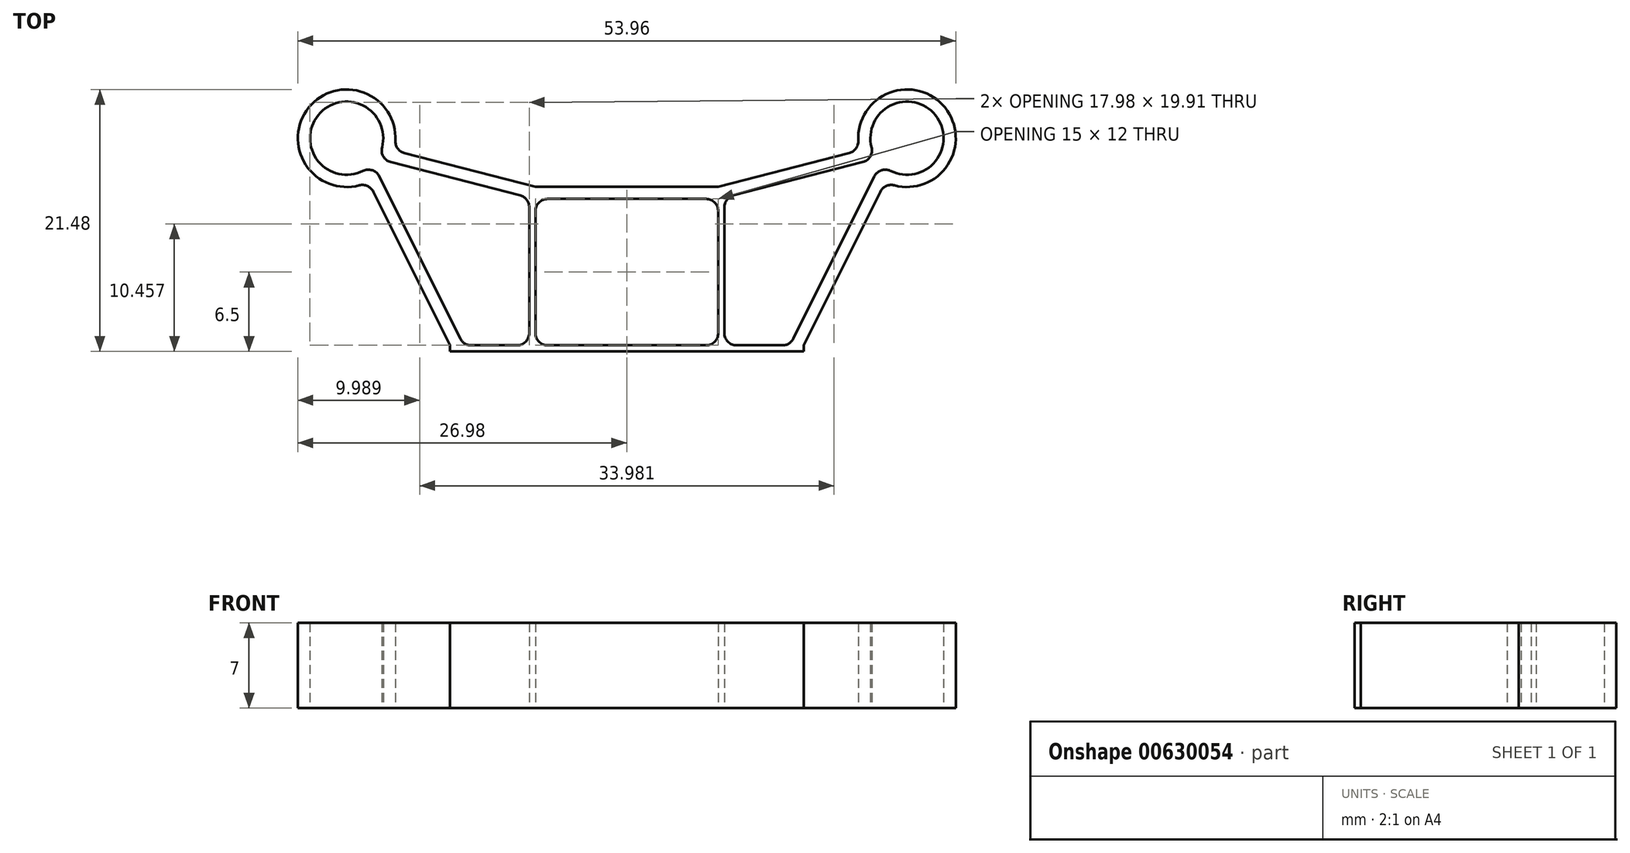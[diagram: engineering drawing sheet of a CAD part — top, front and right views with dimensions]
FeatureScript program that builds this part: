
annotation { "Feature Type Name" : "Feature", "Feature Type Description" : "" }
export const myFeature = defineFeature(function(context is Context, id is Id, definition is map)
    precondition{}
    {
        {
            var Q0;
            Q0=qCreatedBy(makeId("Top.planeOp"),FACE);
            var sketch = newSketch(context, id + "F0", { "sketchPlane" : qUnion([Q0])});
            skCircle(sketch, "E0", {"center": v(0, 0) * mm, "radius": 32.5 * mm, "construction": true});
            skLineSegment(sketch, "E1", {"start": v(0, 0) * mm, "end": v(35.36, 35.36) * mm, "construction": true});
            skArc(sketch, "E2", {"start": v(20.82, 20.9) * mm, "mid": v(25.31, 24.87) * mm, "end": v(20.5, 21.3) * mm});
            skArc(sketch, "E3.0", {"start": v(21.2, 19.4) * mm, "mid": v(26.1, 25.5) * mm, "end": v(19.1, 21.98) * mm});
            skLineSegment(sketch, "E4.bottom", {"start": v(22.5, -5.5) * mm, "end": v(-22.5, -5.5) * mm, "construction": true});
            skLineSegment(sketch, "E4.top", {"start": v(14.5, 5.5) * mm, "end": v(0, 5.5) * mm});
            skLineSegment(sketch, "E4.left", {"start": v(22.5, -5.5) * mm, "end": v(22.5, 6) * mm, "construction": true});
            skLineSegment(sketch, "E4.right", {"start": v(-22.5, -5.5) * mm, "end": v(-22.5, 5.5) * mm, "construction": true});
            skLineSegment(sketch, "E5.0", {"start": v(14.5, -5.5) * mm, "end": v(14.5, 6) * mm, "construction": true});
            skLineSegment(sketch, "E6.0", {"start": v(14.5, 6) * mm, "end": v(0, 6) * mm});
            skLineSegment(sketch, "E7", {"start": v(0, 0) * mm, "end": v(0, 47.28) * mm, "construction": true});
            skPoint(sketch, "E7.endSnap0", {"position": v(0, 18) * mm});
            skLineSegment(sketch, "E8.0", {"start": v(7.5, 0) * mm, "end": v(7.5, 5.5) * mm, "construction": true});
            skLineSegment(sketch, "E9", {"start": v(14.5, 6) * mm, "end": v(21.2, 19.4) * mm});
            skLineSegment(sketch, "E10", {"start": v(7.5, 19) * mm, "end": v(19.1, 21.98) * mm});
            skLineSegment(sketch, "E11.0", {"start": v(13.38, 6) * mm, "end": v(20.82, 20.9) * mm});
            skLineSegment(sketch, "E12.trimOffspring", {"start": v(7.5, 19) * mm, "end": v(0, 19) * mm});
            skLineSegment(sketch, "E13.trimOffspring", {"start": v(7.63, 18) * mm, "end": v(0, 18) * mm});
            skPoint(sketch, "E14.0.start.orphan", {"position": v(22.5, 18) * mm});
            skPoint(sketch, "E15.orphan", {"position": v(-22.5, 18) * mm});
            skLineSegment(sketch, "E16", {"start": v(0, 18) * mm, "end": v(0, 19) * mm});
            skPoint(sketch, "E17.orphan", {"position": v(22.5, 5.5) * mm});
            skLineSegment(sketch, "E18", {"start": v(14.5, 6) * mm, "end": v(14.5, 5.5) * mm});
            skLineSegment(sketch, "E19", {"start": v(0, 6) * mm, "end": v(0, 5.5) * mm});
            skLineSegment(sketch, "E20.trimOffspring", {"start": v(8, 6) * mm, "end": v(8, 18.1) * mm});
            skLineSegment(sketch, "E21", {"start": v(7.63, 18) * mm, "end": v(20.5, 21.3) * mm});
            skLineSegment(sketch, "E22.trimOffspring", {"start": v(7.5, 19) * mm, "end": v(7.5, 47.28) * mm, "construction": true});
            skLineSegment(sketch, "E23.trimOffspring", {"start": v(7.5, 6) * mm, "end": v(7.5, 18) * mm});
            skSolve(sketch);
        }
        {
            var Q0;
            {var subQ6=sQuery(id+"F0.wireOp",EDGE,"E2");Q0=makeQuery(id+"F0.imprint","IMPRINT",FACE,{"disambiguationData":[TD([[makeQuery(id+"F0.imprint","IMPRINT",EDGE,{"derivedFrom":subQ6}),-1.0]])]});}
            var Q1;
            Q1=makeQuery(id+"F0.imprint","IMPRINT",FACE,{"disambiguationData":[TD([[makeQuery(id+"F0.imprint","IMPRINT",EDGE,{"derivedFrom":sQuery(id+"F0.wireOp",EDGE,"E4.top")}),-1.0]])]});
            var Q2;
            {var subQ3=sQuery(id+"F0.wireOp",EDGE,"E20.trimOffspring");Q2=makeQuery(id+"F0.imprint","IMPRINT",FACE,{"disambiguationData":[TD([[makeQuery(id+"F0.imprint","IMPRINT",EDGE,{"derivedFrom":subQ3}),1.0]])]});}
            extrude(context, id + "F1", {"entities" : qUnion([Q0, Q1, Q2]), "depth" : 7 * mm, "offsetDistance" : 25 * mm});
        }
        {
            var Q0;
            Q0=makeQuery(id+"F1.opExtrude","SWEPT_EDGE",EDGE,{"disambiguationData":[OSD([sQuery(id+"F0.wireOp",EDGE,"E3.0"),sQuery(id+"F0.wireOp",EDGE,"E9")])]});
            var Q1;
            Q1=makeQuery(id+"F1.opExtrude","SWEPT_EDGE",EDGE,{"disambiguationData":[OSD([sQuery(id+"F0.wireOp",EDGE,"E2"),sQuery(id+"F0.wireOp",EDGE,"E11.0")])]});
            var Q2;
            Q2=makeQuery(id+"F1.opExtrude","SWEPT_EDGE",EDGE,{"disambiguationData":[OSD([sQuery(id+"F0.wireOp",EDGE,"E2"),sQuery(id+"F0.wireOp",EDGE,"E21")])]});
            var Q3;
            Q3=makeQuery(id+"F1.opExtrude","SWEPT_EDGE",EDGE,{"disambiguationData":[OSD([sQuery(id+"F0.wireOp",EDGE,"E3.0"),sQuery(id+"F0.wireOp",EDGE,"E10")])]});
            fillet(context, id + "F2", {"entities" : qUnion([Q0, Q1, Q2, Q3]), "radius" : 1 * mm, "tangentPropagation" : true, "allowEdgeOverflow" : false});
        }
        {
            var Q0;
            Q0=makeQuery(id+"F1.opExtrude","SWEPT_EDGE",EDGE,{"disambiguationData":[OSD([sQuery(id+"F0.wireOp",EDGE,"E20.trimOffspring"),sQuery(id+"F0.wireOp",EDGE,"E21")])]});
            var Q1;
            Q1=makeQuery(id+"F1.opExtrude","SWEPT_EDGE",EDGE,{"disambiguationData":[OSD([sQuery(id+"F0.wireOp",EDGE,"E6.0"),sQuery(id+"F0.wireOp",EDGE,"E11.0")])]});
            var Q2;
            Q2=makeQuery(id+"F1.opExtrude","SWEPT_EDGE",EDGE,{"disambiguationData":[OSD([sQuery(id+"F0.wireOp",EDGE,"E6.0"),sQuery(id+"F0.wireOp",EDGE,"E20.trimOffspring")])]});
            var Q3;
            Q3=makeQuery(id+"F1.opExtrude","SWEPT_EDGE",EDGE,{"disambiguationData":[OSD([sQuery(id+"F0.wireOp",EDGE,"E13.trimOffspring"),sQuery(id+"F0.wireOp",EDGE,"E23.trimOffspring")])]});
            var Q4;
            Q4=makeQuery(id+"F1.opExtrude","SWEPT_EDGE",EDGE,{"disambiguationData":[OSD([sQuery(id+"F0.wireOp",EDGE,"E6.0"),sQuery(id+"F0.wireOp",EDGE,"E23.trimOffspring")])]});
            fillet(context, id + "F3", {"entities" : qUnion([Q0, Q1, Q2, Q3, Q4]), "radius" : 1 * mm, "tangentPropagation" : true, "allowEdgeOverflow" : false});
        }
        {
            var Q0;
            Q0=makeQuery(id+"F1.opExtrude","SWEPT_BODY",BODY,{"disambiguationData":[OSD([sQuery(id+"F0.wireOp",EDGE,"E2"),sQuery(id+"F0.wireOp",EDGE,"E3.0"),sQuery(id+"F0.wireOp",EDGE,"E4.top"),sQuery(id+"F0.wireOp",EDGE,"E6.0"),sQuery(id+"F0.wireOp",EDGE,"E9"),sQuery(id+"F0.wireOp",EDGE,"E10"),sQuery(id+"F0.wireOp",EDGE,"E11.0"),sQuery(id+"F0.wireOp",EDGE,"E12.trimOffspring"),sQuery(id+"F0.wireOp",EDGE,"E13.trimOffspring"),sQuery(id+"F0.wireOp",EDGE,"E16"),sQuery(id+"F0.wireOp",EDGE,"E18"),sQuery(id+"F0.wireOp",EDGE,"E19"),sQuery(id+"F0.wireOp",EDGE,"E20.trimOffspring"),sQuery(id+"F0.wireOp",EDGE,"E21"),sQuery(id+"F0.wireOp",EDGE,"E23.trimOffspring")])]});
            var Q1;
            Q1=qCreatedBy(makeId("Right.planeOp"),FACE);
            mirror(context, id + "F4", {"operationType" : NewBodyOperationType.ADD, "entities" : qUnion([Q0]), "mirrorPlane" : qUnion([Q1])});
        }
    });
